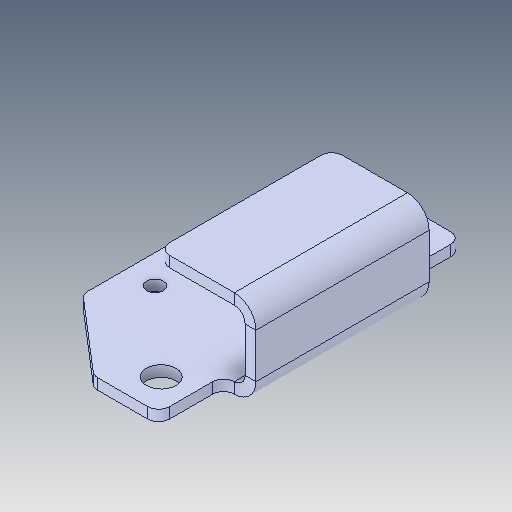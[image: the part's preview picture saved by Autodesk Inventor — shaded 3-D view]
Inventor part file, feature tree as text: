
AUTODESK INVENTOR PART (.ipt)
format: ipt  version: 2023.5 (Build 275446000, 446)  size: 119,808 bytes
history: native  units: in
note: dims shown in document units (in); Inventor stores cm internally (conversion verified against a paired STEP export)
features: fillet x1
ambient origin geometry x8: Origin, YZ Plane, XZ Plane, XY Plane, X Axis, Y Axis, Z Axis, Center Point
bodies: Solid1 (feature_tree)
feature tree (1):
  fillet  "Fillet1"  [1 undecoded]
note: 1 required parameter value undecoded (feature->parameter linkage not recoverable at this tier; creation-order binding heuristic only, values carry confidence <= 0.55)
